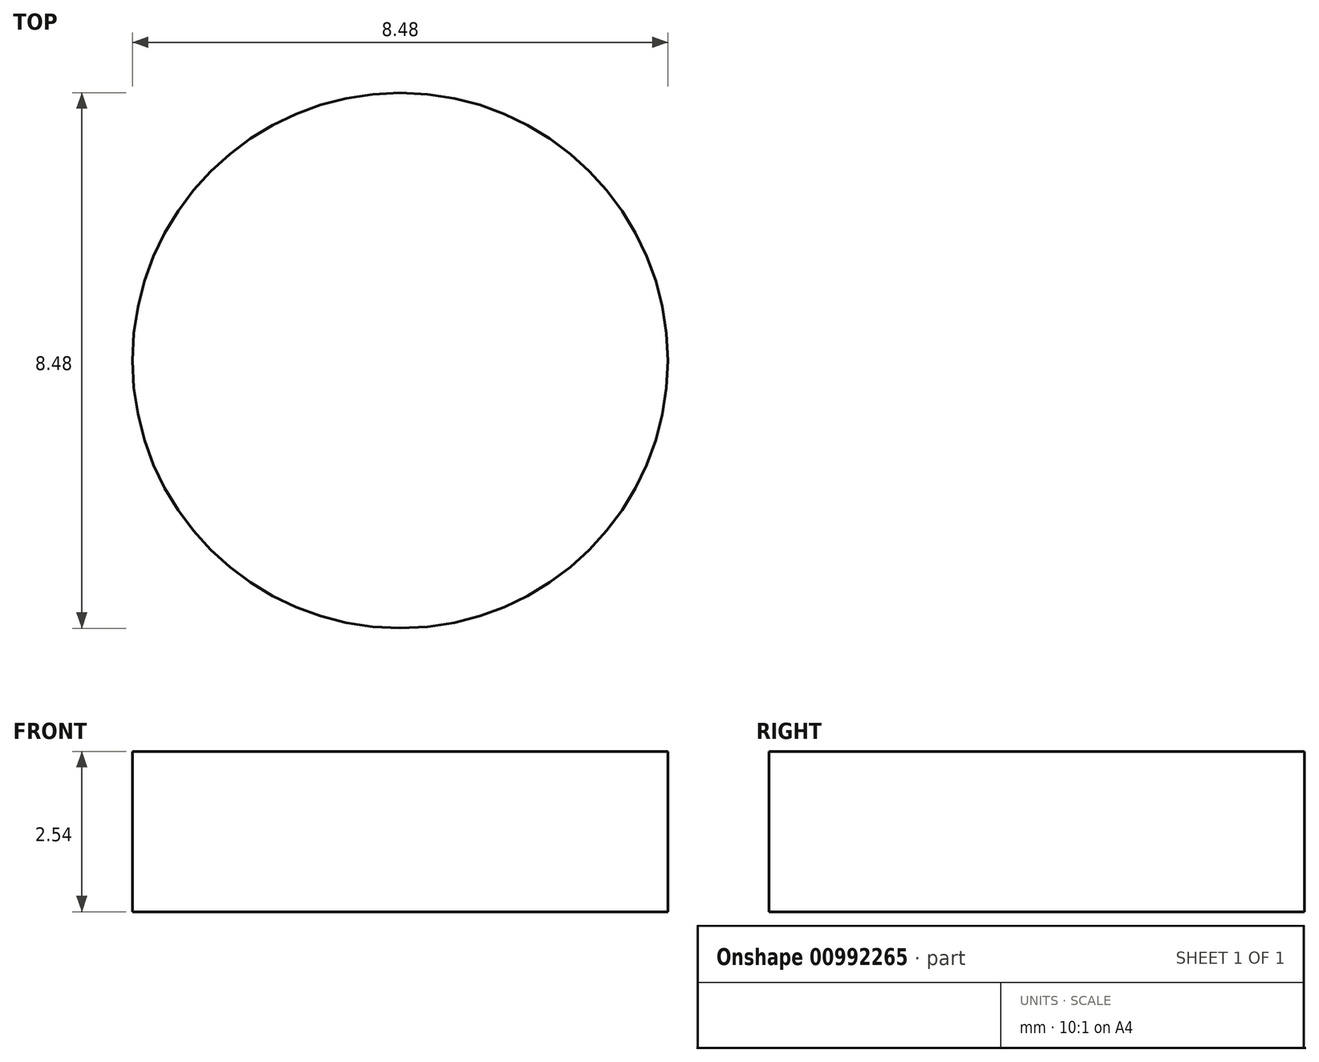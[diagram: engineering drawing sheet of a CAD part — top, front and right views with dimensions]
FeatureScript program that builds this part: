
annotation { "Feature Type Name" : "Feature", "Feature Type Description" : "" }
export const myFeature = defineFeature(function(context is Context, id is Id, definition is map)
    precondition{}
    {
        {
            var Q0;
            Q0=qCreatedBy(makeId("Top.planeOp"),FACE);
            var sketch = newSketch(context, id + "F0", { "sketchPlane" : qUnion([Q0])});
            skCircle(sketch, "E0", {"center": v(0, 0) * mm, "radius": 4.24 * mm});
            skSolve(sketch);
        }
        {
            var Q0;
            Q0=makeQuery(id+"F0.imprint","IMPRINT",FACE,{"disambiguationData":[TD([[makeQuery(id+"F0.imprint","IMPRINT",EDGE,{"derivedFrom":sQuery(id+"F0.wireOp",EDGE,"E0")}),1.0]])]});
            extrude(context, id + "F1", {"entities" : qUnion([Q0]), "depth" : 2.54 * mm, "offsetDistance" : 25.4 * mm});
        }
    });
